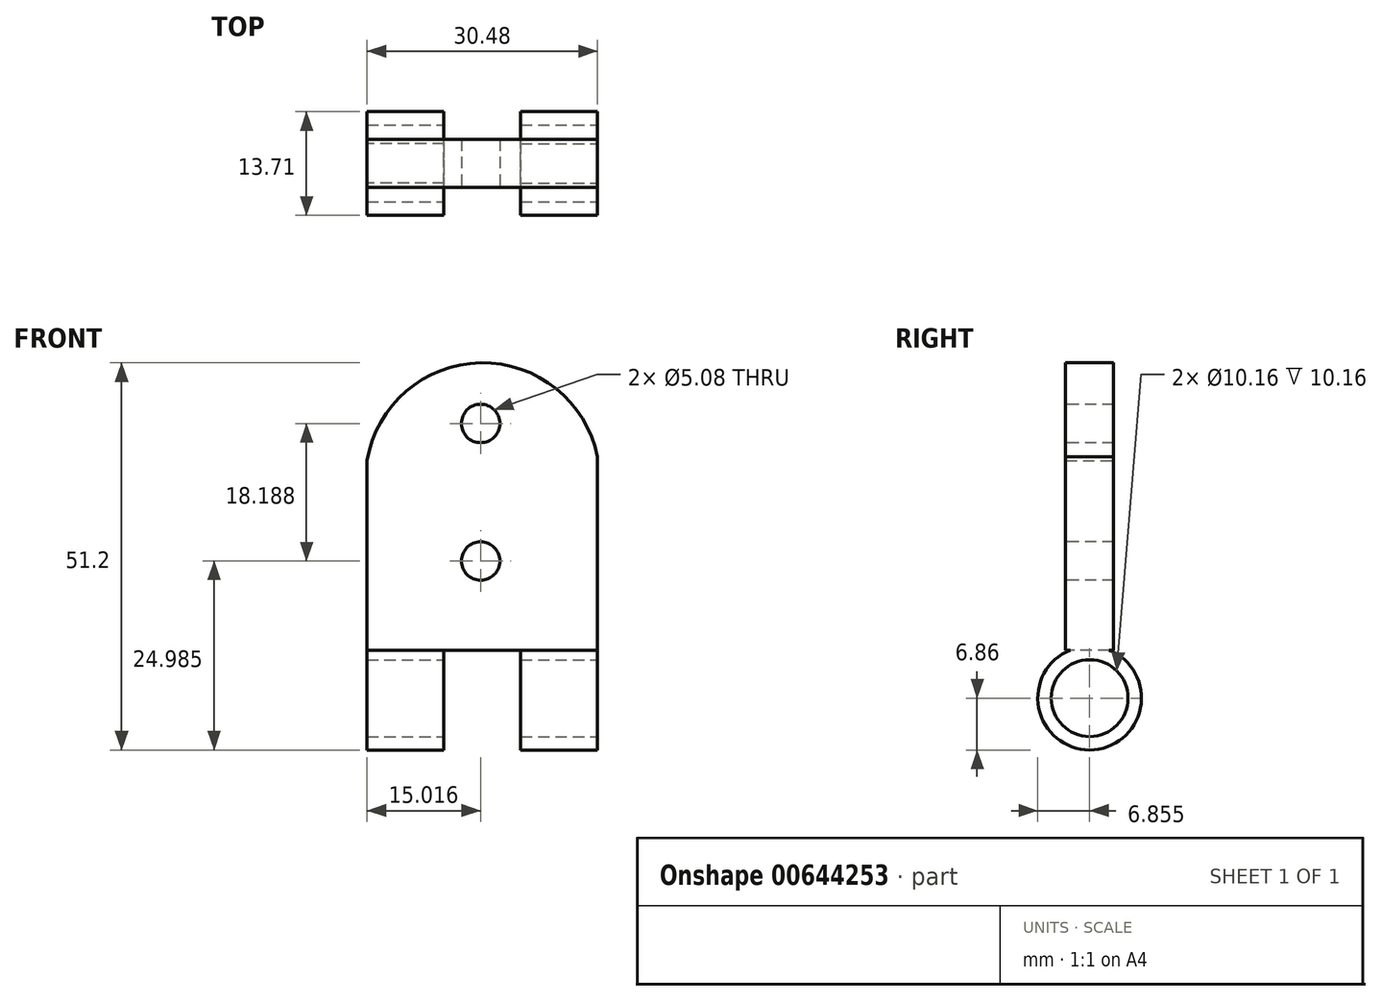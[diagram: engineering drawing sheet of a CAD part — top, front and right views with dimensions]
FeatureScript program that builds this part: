
annotation { "Feature Type Name" : "Feature", "Feature Type Description" : "" }
export const myFeature = defineFeature(function(context is Context, id is Id, definition is map)
    precondition{}
    {
        {
            var Q0;
            Q0=qCreatedBy(makeId("Front.planeOp"),FACE);
            var sketch = newSketch(context, id + "F0", { "sketchPlane" : qUnion([Q0])});
            skLineSegment(sketch, "E0.bottom", {"start": v(0, 0) * mm, "end": v(30.48, 0) * mm});
            skLineSegment(sketch, "E0.top", {"start": v(0, 38.1) * mm, "end": v(30.48, 38.1) * mm});
            skLineSegment(sketch, "E0.left", {"start": v(0, 0) * mm, "end": v(0, 38.1) * mm});
            skLineSegment(sketch, "E0.right", {"start": v(30.48, 0) * mm, "end": v(30.48, 38.1) * mm});
            skArc(sketch, "E1", {"start": v(30.48, 25.58) * mm, "mid": v(15.02, 38) * mm, "end": v(0, 25.04) * mm});
            skSolve(sketch);
        }
        {
            var Q0;
            {var subQ0=sQuery(id+"F0.wireOp",EDGE,"E0.bottom");Q0=makeQuery(id+"F0.imprint","IMPRINT",FACE,{"disambiguationData":[TD([[makeQuery(id+"F0.imprint","IMPRINT",EDGE,{"derivedFrom":subQ0}),1.0]])]});}
            extrude(context, id + "F1", {"entities" : qUnion([Q0]), "depth" : 6.35 * mm, "offsetDistance" : 25.4 * mm});
        }
        {
            var Q0;
            Q0=makeQuery(id+"F1.opExtrude","SWEPT_FACE",FACE,{"disambiguationData":[OSD([sQuery(id+"F0.wireOp",EDGE,"E0.right")])]});
            var sketch = newSketch(context, id + "F2", { "sketchPlane" : qUnion([Q0])});
            skCircle(sketch, "E2", {"center": v(-3.18, -6.35) * mm, "radius": 6.86 * mm});
            skPoint(sketch, "E2.centerSnap0", {"position": v(-3.18, 0) * mm});
            skSolve(sketch);
        }
        {
            var Q0;
            Q0 = qSketchRegion(id + "F2", true);
            extrude(context, id + "F3", {"entities" : qUnion([Q0]), "operationType" : NewBodyOperationType.ADD, "oppositeDirection" : true, "depth" : 10.16 * mm, "offsetDistance" : 25.4 * mm});
        }
        {
            var Q0;
            Q0=makeQuery(id+"F1.opExtrude","SWEPT_FACE",FACE,{"disambiguationData":[OSD([sQuery(id+"F0.wireOp",EDGE,"E0.left")])]});
            var sketch = newSketch(context, id + "F4", { "sketchPlane" : qUnion([Q0])});
            skCircle(sketch, "E3", {"center": v(3.18, -6.35) * mm, "radius": 6.86 * mm});
            skPoint(sketch, "E3.centerSnap0", {"position": v(3.18, 0) * mm});
            skSolve(sketch);
        }
        {
            var Q0;
            Q0 = qSketchRegion(id + "F4", true);
            extrude(context, id + "F5", {"entities" : qUnion([Q0]), "operationType" : NewBodyOperationType.ADD, "oppositeDirection" : true, "depth" : 10.16 * mm, "offsetDistance" : 25.4 * mm});
        }
        {
            var Q0;
            Q0=makeQuery(id+"F3.boolean.opBoolean","MERGE",FACE,{"derivedFrom":[makeQuery(id+"F1.opExtrude","SWEPT_FACE",FACE,{"disambiguationData":[OSD([sQuery(id+"F0.wireOp",EDGE,"E0.right")])]}),makeQuery(id+"F3.opExtrude","CAP_FACE",FACE,{"disambiguationData":[OSD([sQuery(id+"F2.wireOp",EDGE,"E2")])],"isStart":true})]});
            var sketch = newSketch(context, id + "F6", { "sketchPlane" : qUnion([Q0])});
            skCircle(sketch, "E4", {"center": v(-3.18, -6.35) * mm, "radius": 5.08 * mm});
            skSolve(sketch);
        }
        {
            var Q0;
            Q0 = qSketchRegion(id + "F6", true);
            extrude(context, id + "F7", {"entities" : qUnion([Q0]), "operationType" : NewBodyOperationType.REMOVE, "endBound" : BoundingType.THROUGH_ALL, "oppositeDirection" : true, "depth" : 25.4 * mm, "offsetDistance" : 25.4 * mm});
        }
        {
            var Q0;
            Q0=makeQuery(id+"F1.opExtrude","CAP_FACE",FACE,{"disambiguationData":[OSD([sQuery(id+"F0.wireOp",EDGE,"E0.bottom"),sQuery(id+"F0.wireOp",EDGE,"E0.left"),sQuery(id+"F0.wireOp",EDGE,"E0.right"),sQuery(id+"F0.wireOp",EDGE,"E1")])],"isStart":false});
            var sketch = newSketch(context, id + "F8", { "sketchPlane" : qUnion([Q0])});
            skCircle(sketch, "E5", {"center": v(15.02, 29.96) * mm, "radius": 2.54 * mm});
            skPoint(sketch, "E5.centerSnap0", {"position": v(15.02, 38) * mm});
            skCircle(sketch, "E6", {"center": v(15.02, 11.77) * mm, "radius": 2.54 * mm});
            skSolve(sketch);
        }
        {
            var Q0;
            Q0 = qSketchRegion(id + "F8", true);
            extrude(context, id + "F9", {"entities" : qUnion([Q0]), "operationType" : NewBodyOperationType.REMOVE, "oppositeDirection" : true, "depth" : 25.4 * mm, "offsetDistance" : 25.4 * mm});
        }
    });
